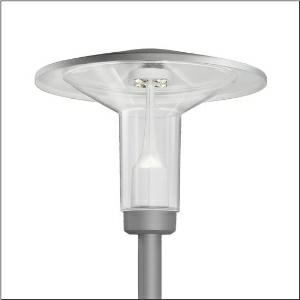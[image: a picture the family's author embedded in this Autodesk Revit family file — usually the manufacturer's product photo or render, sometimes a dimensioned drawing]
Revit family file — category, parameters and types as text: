
# Revit family: laterne_iq___st1_2a_5xa5255af14h_83bc
name_source: partatom
category: Lighting Fixtures
units: mm (PartAtom-declared; Revit-internal decimal feet)

## family parameters
Cut with Voids When Loaded = No
Host = Face
Light Source = No
Part Type = Normal
Room Calculation Point = No
Round Connector Dimension = Use Diameter
Shared = No

## types (1)
- --- (1 x LED, 1540 lm, 12.9 W, 2200K)
    Apparent Load = 13 VA
    CIE Flux Codes = 25 63 94 98 100
    Color Rendering = 70
    Color Temperature = 2200K
    Default Elevation = 1800 mm
    Description = Lantern iQ, mast luminaire, Module 540 iQ-SR, primary light control with 3 zone facetted reflector, of plastic, silver coated, highly specular, structured, primary optical cover: cover, of PMMA, transparent, light distribution: ST1.2a, light emission: direct distribution, primary light characteristic: asymmetric, installation type: post-top, LED, High Power LED, rated luminous flux: 1.540lm, luminous efficacy: 119lm/W, light colour: 722, colour temperature: 2200K, control gear: iQ Street-Remote, control: pre-setting: logarithmic dimming characteristic, Street-Remote, Auto-Match, Temp-Guard, Lumen-Switch, Night-Set, Smart-Wire, Light-Fading, Desk-Remote (wireless, voltage-free reading and setting of iQ features in the workshop via application-optimized NFC function/RFID function), optimised constant luminous flux control (CLO 2.0), with terminal, 6-pole, max. 2.5mm², mains connection: 230..240V, AC, 50/60Hz, start of lifetime: 13W, end of service life: 13W, reduction: 6W, luminaire housing, upper part, of glass-fibre reinforced polyester, coated, Siteco® metallic grey (DB 702S), diameter: 750mm, height: 583mm, spigot size: d x l = 76 x 70mm (post-top) | with reducer (optional accessory) 60 x 70mm, mounting height: 3..5m, post-top mast mounting element, of diecast aluminium, coated, Siteco® metallic grey (DB 702S), Module 540 iQ-SR, traffic white (RAL 9016), equipment: standard, protection rating (complete): IP65, insulation class (complete): insulation class II (safety insulation), certification: CE, ENEC, VDE, packaging unit: 1 piece

Light Distribution: ST1.2a
    Height = 583 mm
    Lamp = 1 x LED
    Lamp Light Flux = 1540 lm
    Lamp Power = 12.9 W
    Lamp count = 1
    Length = 750 mm
    Luminous efficacy = 119 lm/W
    Manufacturer = Siteco
    ModVariant = No
    Model = 5XA5255AF14H
    Number of Poles = 1
    OnlyDefault = Yes
    Power Factor = 1
    Product Name = Laterne iQ | ST1.2a
    Product group = mast luminaire | pylon top
    ProductGroupID = 6100
    Protection Class = Protection class II
    Protection Degree = IP 65
    RLX_Detail_Level = 1
    RLX_Emergency_Light_Flux = 0 lm
    RLX_Emergency_Type = 0
    RLX_Emergency_Type_DB = No
    RlxData = <blob elided: 90397 chars, md5=6c020d66>
    Socket = socket
    Standby Power = 0 W
    System Light Flux = 1540 lm
    System Power = 13 W
    Type Comments = factory setting: luminous flux: 100 % | dim-lin: 254 | 516 mA
    Type Image = l_1006050.jpg
    URL = http://relux.com
    VarID = @adj_182133
    Voltage = 0 V
    Weight = 0.00 kg
    Width = 0 mm  [stored 0 ft]

note: [stored X ft] marks values corroborated as IEEE doubles in the binary element streams (Revit-internal decimal feet)

## geometry (parser evidence)
native form markers: Blend x4, Sweep x12
no freeform markers — native parametric forms only
